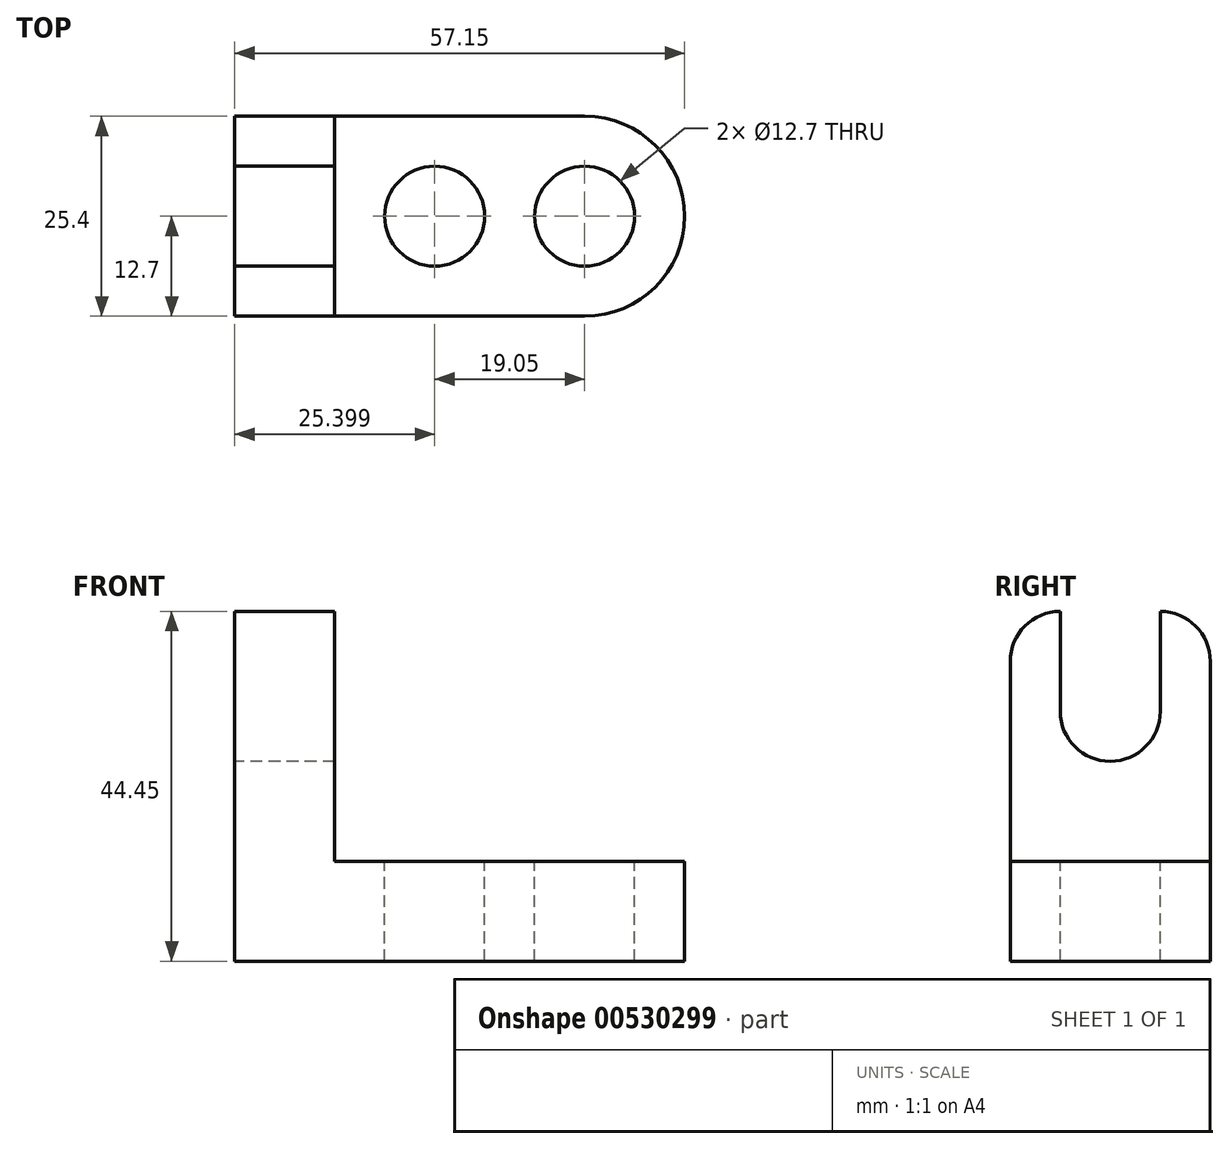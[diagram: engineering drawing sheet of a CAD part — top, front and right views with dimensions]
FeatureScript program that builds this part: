
annotation { "Feature Type Name" : "Feature", "Feature Type Description" : "" }
export const myFeature = defineFeature(function(context is Context, id is Id, definition is map)
    precondition{}
    {
        {
            var Q0;
            Q0=qCreatedBy(makeId("Front.planeOp"),FACE);
            var sketch = newSketch(context, id + "F0", { "sketchPlane" : qUnion([Q0])});
            skLineSegment(sketch, "E0", {"start": v(-54.1, 44.45) * mm, "end": v(-54.1, 0) * mm});
            skLineSegment(sketch, "E1", {"start": v(-54.1, 0) * mm, "end": v(3.06, 0) * mm});
            skLineSegment(sketch, "E2", {"start": v(-41.4, 12.7) * mm, "end": v(-41.4, 44.45) * mm});
            skLineSegment(sketch, "E3", {"start": v(-41.4, 44.45) * mm, "end": v(-54.1, 44.45) * mm});
            skLineSegment(sketch, "E4", {"start": v(-41.4, 12.7) * mm, "end": v(3.06, 12.7) * mm});
            skLineSegment(sketch, "E5", {"start": v(3.06, 12.7) * mm, "end": v(3.06, 0) * mm});
            skSolve(sketch);
        }
        {
            var Q0;
            Q0=makeQuery(id+"F0.imprint","IMPRINT",FACE,{"disambiguationData":[TD([[makeQuery(id+"F0.imprint","IMPRINT",EDGE,{"derivedFrom":sQuery(id+"F0.wireOp",EDGE,"E0")}),1.0]])]});
            extrude(context, id + "F1", {"entities" : qUnion([Q0]), "depth" : 25.4 * mm, "offsetDistance" : 25.4 * mm});
        }
        {
            var Q0;
            Q0=makeQuery(id+"F1.opExtrude","SWEPT_FACE",FACE,{"disambiguationData":[OSD([sQuery(id+"F0.wireOp",EDGE,"E4")])]});
            var sketch = newSketch(context, id + "F2", { "sketchPlane" : qUnion([Q0])});
            skCircle(sketch, "E6", {"center": v(-28.7, -12.7) * mm, "radius": 6.35 * mm});
            skCircle(sketch, "E7", {"center": v(-9.64, -12.7) * mm, "radius": 6.35 * mm});
            skArc(sketch, "E8", {"start": v(-9.64, -25.4) * mm, "mid": v(3.06, -12.7) * mm, "end": v(-9.64, 0) * mm});
            skSolve(sketch);
        }
        {
            var Q0;
            Q0=makeQuery(id+"F2.imprint","IMPRINT",FACE,{"disambiguationData":[TD([[makeQuery(id+"F2.imprint","IMPRINT",EDGE,{"derivedFrom":sQuery(id+"F2.wireOp",EDGE,"E6")}),1.0]])]});
            var Q1;
            Q1=makeQuery(id+"F2.imprint","IMPRINT",FACE,{"disambiguationData":[TD([[makeQuery(id+"F2.imprint","IMPRINT",EDGE,{"derivedFrom":sQuery(id+"F2.wireOp",EDGE,"E7")}),1.0]])]});
            var Q2;
            {var subQ0=sQuery(id+"F2.wireOp",EDGE,"E8");var subQ1=sQuery(id+"F0.wireOp",EDGE,"E4");var subQ2=makeQuery(id+"F1.opExtrude","CAP_EDGE",EDGE,{"disambiguationData":[OSD([subQ1])],"isStart":true});var subQ3=makeQuery(id+"F2.imprint","INTERSECT",VERTEX,{"derivedFrom":[subQ2,subQ0]});Q2=makeQuery(id+"F2.imprint","IMPRINT",FACE,{"disambiguationData":[TD([[makeQuery(id+"F2.imprint","IMPRINT",EDGE,{"disambiguationData":[TD([[subQ3,1.0]])],"derivedFrom":subQ0}),-1.0]])]});}
            var Q3;
            {var subQ0=sQuery(id+"F2.wireOp",EDGE,"E8");var subQ1=sQuery(id+"F0.wireOp",EDGE,"E4");var subQ2=makeQuery(id+"F1.opExtrude","CAP_EDGE",EDGE,{"disambiguationData":[OSD([subQ1])],"isStart":false});var subQ3=makeQuery(id+"F2.imprint","INTERSECT",VERTEX,{"derivedFrom":[subQ2,subQ0]});Q3=makeQuery(id+"F2.imprint","IMPRINT",FACE,{"disambiguationData":[TD([[makeQuery(id+"F2.imprint","IMPRINT",EDGE,{"disambiguationData":[TD([[subQ3,-1.0]])],"derivedFrom":subQ0}),-1.0]])]});}
            extrude(context, id + "F3", {"entities" : qUnion([Q0, Q1, Q2, Q3]), "operationType" : NewBodyOperationType.REMOVE, "endBound" : BoundingType.THROUGH_ALL, "oppositeDirection" : true, "depth" : 25.4 * mm, "offsetDistance" : 25.4 * mm});
        }
        {
            var Q0;
            Q0=makeQuery(id+"F1.opExtrude","SWEPT_FACE",FACE,{"disambiguationData":[OSD([sQuery(id+"F0.wireOp",EDGE,"E0")])]});
            var sketch = newSketch(context, id + "F4", { "sketchPlane" : qUnion([Q0])});
            skCircle(sketch, "E9", {"center": v(12.7, 31.75) * mm, "radius": 6.35 * mm});
            skLineSegment(sketch, "E10", {"start": v(6.35, 31.75) * mm, "end": v(6.35, 44.45) * mm});
            skLineSegment(sketch, "E11", {"start": v(19.05, 31.75) * mm, "end": v(19.05, 44.45) * mm});
            skLineSegment(sketch, "E12", {"start": v(12.7, 31.75) * mm, "end": v(19.05, 31.75) * mm});
            skLineSegment(sketch, "E13", {"start": v(0, 44.45) * mm, "end": v(0, 38.1) * mm});
            skPoint(sketch, "E13.endSnap0", {"position": v(19.05, 38.1) * mm});
            skLineSegment(sketch, "E14", {"start": v(25.4, 44.45) * mm, "end": v(25.4, 38.1) * mm});
            skArc(sketch, "E15", {"start": v(6.35, 44.45) * mm, "mid": v(1.86, 42.6) * mm, "end": v(0, 38.1) * mm});
            skArc(sketch, "E16", {"start": v(25.4, 38.1) * mm, "mid": v(23.54, 42.59) * mm, "end": v(19.05, 44.45) * mm});
            skSolve(sketch);
        }
        {
            var Q0;
            {var subQ0=sQuery(id+"F4.wireOp",EDGE,"E9");var subQ1=makeQuery(id+"F4.imprint","INTERSECT",VERTEX,{"derivedFrom":[subQ0,sQuery(id+"F4.wireOp",EDGE,"E10")]});Q0=makeQuery(id+"F4.imprint","IMPRINT",FACE,{"disambiguationData":[TD([[makeQuery(id+"F4.imprint","IMPRINT",EDGE,{"disambiguationData":[TD([[subQ1,1.0]])],"derivedFrom":subQ0}),1.0]])]});}
            var Q1;
            {var subQ0=sQuery(id+"F4.wireOp",EDGE,"E13");Q1=makeQuery(id+"F4.imprint","IMPRINT",FACE,{"disambiguationData":[TD([[makeQuery(id+"F4.imprint","IMPRINT",EDGE,{"derivedFrom":subQ0}),1.0]])]});}
            var Q2;
            {var subQ0=sQuery(id+"F4.wireOp",EDGE,"E14");Q2=makeQuery(id+"F4.imprint","IMPRINT",FACE,{"disambiguationData":[TD([[makeQuery(id+"F4.imprint","IMPRINT",EDGE,{"derivedFrom":subQ0}),-1.0]])]});}
            var Q3;
            {var subQ0=sQuery(id+"F4.wireOp",EDGE,"E10");Q3=makeQuery(id+"F4.imprint","IMPRINT",FACE,{"disambiguationData":[TD([[makeQuery(id+"F4.imprint","IMPRINT",EDGE,{"derivedFrom":subQ0}),-1.0]])]});}
            extrude(context, id + "F5", {"entities" : qUnion([Q0, Q1, Q2, Q3]), "operationType" : NewBodyOperationType.REMOVE, "oppositeDirection" : true, "depth" : 25.4 * mm, "offsetDistance" : 25.4 * mm});
        }
    });
